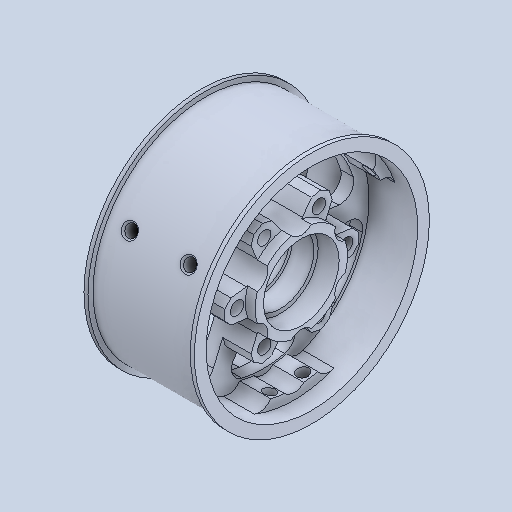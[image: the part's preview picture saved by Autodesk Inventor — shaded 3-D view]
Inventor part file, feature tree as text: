
AUTODESK INVENTOR PART (.ipt)
format: ipt  version: 2024.2 (Build 282272000, 272)  size: 372,224 bytes
history: native  units: in
note: dims shown in document units (in); Inventor stores cm internally (conversion verified against a paired STEP export)
features: mirror x1
ambient origin geometry x8: Origin, YZ Plane, XZ Plane, XY Plane, X Axis, Y Axis, Z Axis, Center Point
bodies: Solid1 (feature_tree)
feature tree (1):
  mirror  "Mirror3"
